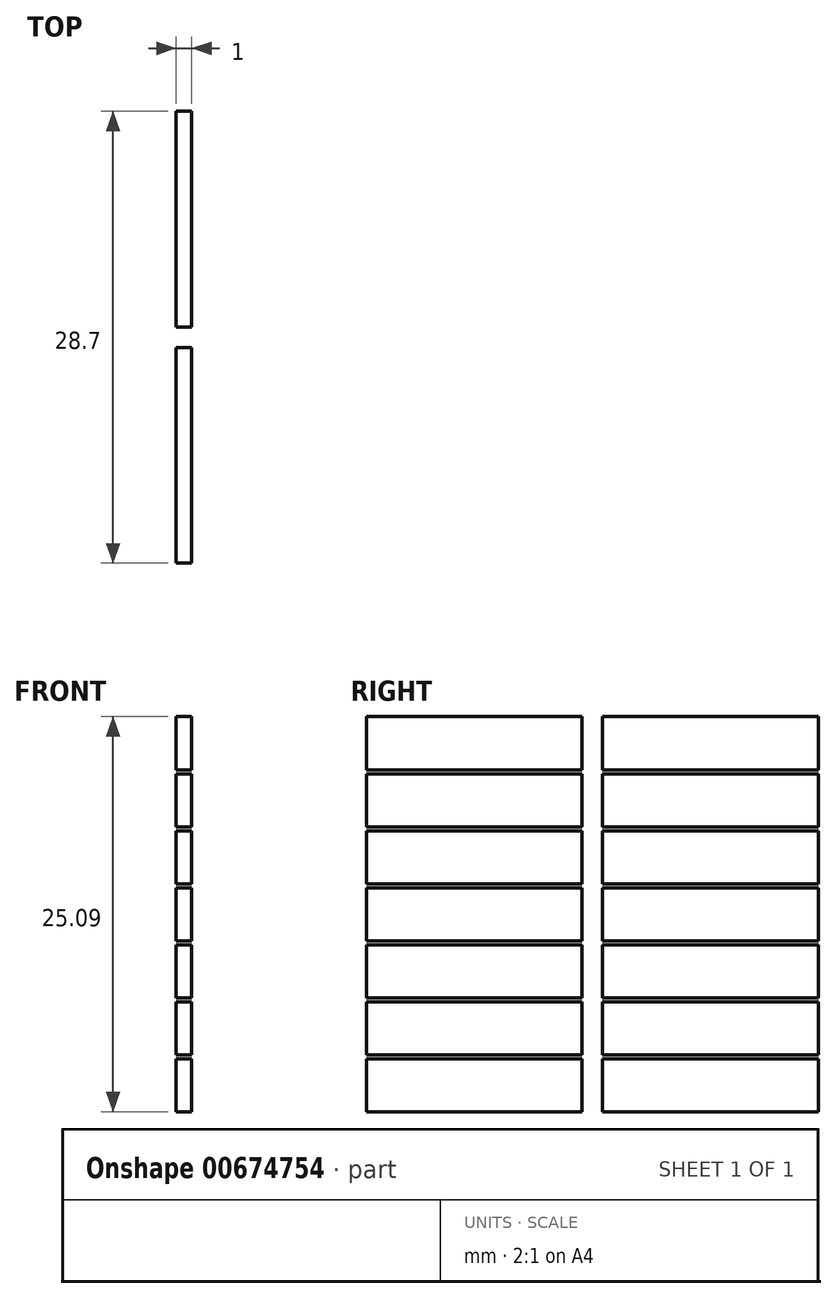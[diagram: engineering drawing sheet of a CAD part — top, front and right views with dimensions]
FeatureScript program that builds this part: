
annotation { "Feature Type Name" : "Feature", "Feature Type Description" : "" }
export const myFeature = defineFeature(function(context is Context, id is Id, definition is map)
    precondition{}
    {
        {
            var Q0;
            Q0=qCreatedBy(makeId("Right.planeOp"),FACE);
            var sketch = newSketch(context, id + "F0", { "sketchPlane" : qUnion([Q0])});
            skPoint(sketch, "E0.0", {"position": v(0, 0) * mm});
            skLineSegment(sketch, "E1.bottom", {"start": v(0, 0) * mm, "end": v(30, 0) * mm});
            skLineSegment(sketch, "E1.top", {"start": v(0, -30) * mm, "end": v(30, -30) * mm});
            skLineSegment(sketch, "E1.left", {"start": v(0, 0) * mm, "end": v(0, -30) * mm});
            skLineSegment(sketch, "E1.right", {"start": v(30, 0) * mm, "end": v(30, -30) * mm});
            skLineSegment(sketch, "E2.1", {"start": v(0.65, -0.65) * mm, "end": v(14.35, -0.65) * mm});
            skLineSegment(sketch, "E2.2", {"start": v(0.65, -0.65) * mm, "end": v(0.65, -2.2) * mm});
            skLineSegment(sketch, "E3", {"start": v(14.35, -2.2) * mm, "end": v(14.35, -0.65) * mm});
            skPoint(sketch, "E4.MirrorP", {"position": v(11.5, 0) * mm});
            skPoint(sketch, "E5.orphan", {"position": v(0, -26.74) * mm});
            skLineSegment(sketch, "E6", {"start": v(0.65, -2.46) * mm, "end": v(0.65, -4.02) * mm});
            skLineSegment(sketch, "E7", {"start": v(0.65, -4.02) * mm, "end": v(14.35, -4.02) * mm});
            skLineSegment(sketch, "E8", {"start": v(14.35, -4.02) * mm, "end": v(14.35, -2.46) * mm});
            skLineSegment(sketch, "E9.0", {"start": v(0.65, -4.27) * mm, "end": v(14.35, -4.27) * mm});
            skLineSegment(sketch, "E10", {"start": v(0.65, -4.27) * mm, "end": v(0.65, -5.83) * mm});
            skLineSegment(sketch, "E11", {"start": v(14.35, -5.83) * mm, "end": v(14.35, -4.27) * mm});
            skLineSegment(sketch, "E12.0", {"start": v(0.65, -7.64) * mm, "end": v(14.35, -7.64) * mm});
            skLineSegment(sketch, "E13", {"start": v(0.65, -6.08) * mm, "end": v(0.65, -7.64) * mm});
            skLineSegment(sketch, "E14", {"start": v(14.35, -6.08) * mm, "end": v(14.35, -7.64) * mm});
            skLineSegment(sketch, "E15.0", {"start": v(0.65, -7.9) * mm, "end": v(14.35, -7.9) * mm});
            skLineSegment(sketch, "E16", {"start": v(0.65, -7.9) * mm, "end": v(0.65, -9.45) * mm});
            skLineSegment(sketch, "E17", {"start": v(14.35, -9.45) * mm, "end": v(14.35, -7.9) * mm});
            skLineSegment(sketch, "E18.0", {"start": v(0.65, -11.26) * mm, "end": v(14.35, -11.26) * mm});
            skLineSegment(sketch, "E19", {"start": v(0.65, -9.7) * mm, "end": v(0.65, -11.26) * mm});
            skLineSegment(sketch, "E20", {"start": v(14.35, -9.7) * mm, "end": v(14.35, -11.26) * mm});
            skLineSegment(sketch, "E21.0", {"start": v(0.65, -11.51) * mm, "end": v(14.35, -11.51) * mm});
            skLineSegment(sketch, "E22", {"start": v(0.65, -11.51) * mm, "end": v(0.65, -13.07) * mm});
            skLineSegment(sketch, "E23", {"start": v(14.35, -13.07) * mm, "end": v(14.35, -11.51) * mm});
            skLineSegment(sketch, "E24.0", {"start": v(0.65, -14.88) * mm, "end": v(14.35, -14.88) * mm});
            skLineSegment(sketch, "E25", {"start": v(0.65, -13.32) * mm, "end": v(0.65, -14.88) * mm});
            skLineSegment(sketch, "E26", {"start": v(14.35, -14.88) * mm, "end": v(14.35, -13.32) * mm});
            skLineSegment(sketch, "E27.0", {"start": v(0.65, -15.13) * mm, "end": v(14.35, -15.13) * mm});
            skLineSegment(sketch, "E28", {"start": v(0.65, -15.13) * mm, "end": v(0.65, -16.7) * mm});
            skLineSegment(sketch, "E29", {"start": v(14.35, -16.7) * mm, "end": v(14.35, -15.13) * mm});
            skLineSegment(sketch, "E30.0", {"start": v(0.65, -18.5) * mm, "end": v(14.35, -18.5) * mm});
            skLineSegment(sketch, "E31", {"start": v(0.65, -16.7) * mm, "end": v(0.65, -18.5) * mm});
            skLineSegment(sketch, "E32", {"start": v(14.35, -18.5) * mm, "end": v(14.35, -16.94) * mm});
            skLineSegment(sketch, "E33.0", {"start": v(0.65, -18.75) * mm, "end": v(14.35, -18.75) * mm});
            skLineSegment(sketch, "E34", {"start": v(0.65, -18.75) * mm, "end": v(0.65, -20.31) * mm});
            skLineSegment(sketch, "E35", {"start": v(14.35, -18.75) * mm, "end": v(14.35, -20.31) * mm});
            skLineSegment(sketch, "E36.0", {"start": v(0.65, -22.12) * mm, "end": v(14.35, -22.12) * mm});
            skLineSegment(sketch, "E37", {"start": v(0.65, -20.56) * mm, "end": v(0.65, -22.12) * mm});
            skLineSegment(sketch, "E38", {"start": v(14.35, -20.56) * mm, "end": v(14.35, -22.12) * mm});
            skLineSegment(sketch, "E39.0", {"start": v(0.65, -22.37) * mm, "end": v(14.35, -22.37) * mm});
            skLineSegment(sketch, "E40", {"start": v(0.65, -22.37) * mm, "end": v(0.65, -23.93) * mm});
            skLineSegment(sketch, "E41", {"start": v(14.35, -22.37) * mm, "end": v(14.35, -23.93) * mm});
            skLineSegment(sketch, "E42.0", {"start": v(0.65, -25.74) * mm, "end": v(14.35, -25.74) * mm});
            skLineSegment(sketch, "E43", {"start": v(0.65, -24.18) * mm, "end": v(0.65, -25.74) * mm});
            skLineSegment(sketch, "E44", {"start": v(14.35, -24.18) * mm, "end": v(14.35, -25.74) * mm});
            skLineSegment(sketch, "E45", {"start": v(0.65, -2.46) * mm, "end": v(0.65, -2.2) * mm});
            skLineSegment(sketch, "E46", {"start": v(14.35, -2.46) * mm, "end": v(14.35, -2.2) * mm});
            skLineSegment(sketch, "E47", {"start": v(0.65, -6.08) * mm, "end": v(0.65, -5.83) * mm});
            skLineSegment(sketch, "E48", {"start": v(14.35, -6.08) * mm, "end": v(14.35, -5.83) * mm});
            skLineSegment(sketch, "E49", {"start": v(14.35, -24.18) * mm, "end": v(14.35, -23.93) * mm});
            skLineSegment(sketch, "E50", {"start": v(0.65, -24.18) * mm, "end": v(0.65, -23.93) * mm});
            skLineSegment(sketch, "E51", {"start": v(0.65, -20.56) * mm, "end": v(0.65, -20.31) * mm});
            skLineSegment(sketch, "E52", {"start": v(14.35, -20.56) * mm, "end": v(14.35, -20.31) * mm});
            skLineSegment(sketch, "E53", {"start": v(14.35, -16.94) * mm, "end": v(14.35, -16.7) * mm});
            skLineSegment(sketch, "E54", {"start": v(14.35, -13.32) * mm, "end": v(14.35, -13.07) * mm});
            skLineSegment(sketch, "E55", {"start": v(0.65, -13.32) * mm, "end": v(0.65, -13.07) * mm});
            skLineSegment(sketch, "E56", {"start": v(0.65, -9.7) * mm, "end": v(0.65, -9.45) * mm});
            skLineSegment(sketch, "E57", {"start": v(14.35, -9.7) * mm, "end": v(14.35, -9.45) * mm});
            skLineSegment(sketch, "E58.MirrorCS", {"start": v(29.35, -0.65) * mm, "end": v(29.35, -2.2) * mm});
            skLineSegment(sketch, "E59.MirrorCS", {"start": v(29.35, -2.46) * mm, "end": v(29.35, -2.2) * mm});
            skLineSegment(sketch, "E60.MirrorCS", {"start": v(29.35, -2.46) * mm, "end": v(29.35, -4.02) * mm});
            skLineSegment(sketch, "E61.MirrorCS", {"start": v(29.35, -20.56) * mm, "end": v(29.35, -22.12) * mm});
            skLineSegment(sketch, "E62.MirrorCS", {"start": v(15.65, -4.02) * mm, "end": v(15.65, -2.46) * mm});
            skLineSegment(sketch, "E63.MirrorCS", {"start": v(29.35, -20.56) * mm, "end": v(29.35, -20.31) * mm});
            skLineSegment(sketch, "E64.MirrorCS", {"start": v(29.35, -7.9) * mm, "end": v(29.35, -9.45) * mm});
            skLineSegment(sketch, "E65.MirrorCS", {"start": v(15.65, -16.7) * mm, "end": v(15.65, -15.13) * mm});
            skLineSegment(sketch, "E66.MirrorCS", {"start": v(29.35, -9.7) * mm, "end": v(29.35, -9.45) * mm});
            skLineSegment(sketch, "E67.MirrorCS", {"start": v(29.35, -6.08) * mm, "end": v(29.35, -5.83) * mm});
            skLineSegment(sketch, "E68.MirrorCS", {"start": v(15.65, -9.7) * mm, "end": v(15.65, -9.45) * mm});
            skLineSegment(sketch, "E69.MirrorCS", {"start": v(15.65, -22.37) * mm, "end": v(15.65, -23.93) * mm});
            skLineSegment(sketch, "E70.MirrorCS", {"start": v(29.35, -24.18) * mm, "end": v(29.35, -23.93) * mm});
            skLineSegment(sketch, "E71.MirrorCS", {"start": v(29.35, -4.27) * mm, "end": v(29.35, -5.83) * mm});
            skLineSegment(sketch, "E72.MirrorCS", {"start": v(15.65, -20.56) * mm, "end": v(15.65, -20.31) * mm});
            skLineSegment(sketch, "E73.MirrorCS", {"start": v(15.65, -9.45) * mm, "end": v(15.65, -7.9) * mm});
            skLineSegment(sketch, "E74.MirrorCS", {"start": v(29.35, -11.51) * mm, "end": v(29.35, -13.07) * mm});
            skLineSegment(sketch, "E75.MirrorCS", {"start": v(29.35, -13.32) * mm, "end": v(29.35, -13.07) * mm});
            skLineSegment(sketch, "E76.MirrorCS", {"start": v(15.65, -6.08) * mm, "end": v(15.65, -7.64) * mm});
            skLineSegment(sketch, "E77.MirrorCS", {"start": v(15.65, -14.88) * mm, "end": v(15.65, -13.32) * mm});
            skLineSegment(sketch, "E78.MirrorCS", {"start": v(29.35, -18.75) * mm, "end": v(29.35, -20.31) * mm});
            skLineSegment(sketch, "E79.MirrorCS", {"start": v(15.65, -24.18) * mm, "end": v(15.65, -23.93) * mm});
            skLineSegment(sketch, "E80.MirrorCS", {"start": v(29.35, -6.08) * mm, "end": v(29.35, -7.64) * mm});
            skLineSegment(sketch, "E81.MirrorCS", {"start": v(29.35, -13.32) * mm, "end": v(29.35, -14.88) * mm});
            skLineSegment(sketch, "E82.MirrorCS", {"start": v(15.65, -6.08) * mm, "end": v(15.65, -5.83) * mm});
            skLineSegment(sketch, "E83.MirrorCS", {"start": v(15.65, -18.5) * mm, "end": v(15.65, -16.94) * mm});
            skLineSegment(sketch, "E84.MirrorCS", {"start": v(29.35, -9.7) * mm, "end": v(29.35, -11.26) * mm});
            skLineSegment(sketch, "E85.MirrorCS", {"start": v(15.65, -13.07) * mm, "end": v(15.65, -11.51) * mm});
            skLineSegment(sketch, "E86.MirrorCS", {"start": v(15.65, -20.56) * mm, "end": v(15.65, -22.12) * mm});
            skLineSegment(sketch, "E87.MirrorCS", {"start": v(15.65, -13.32) * mm, "end": v(15.65, -13.07) * mm});
            skLineSegment(sketch, "E88.MirrorCS", {"start": v(15.65, -5.83) * mm, "end": v(15.65, -4.27) * mm});
            skLineSegment(sketch, "E89.MirrorCS", {"start": v(15.65, -9.7) * mm, "end": v(15.65, -11.26) * mm});
            skLineSegment(sketch, "E90.MirrorCS", {"start": v(29.35, -22.37) * mm, "end": v(29.35, -23.93) * mm});
            skLineSegment(sketch, "E91.MirrorCS", {"start": v(15.65, -18.75) * mm, "end": v(15.65, -20.31) * mm});
            skLineSegment(sketch, "E92.MirrorCS", {"start": v(29.35, -16.7) * mm, "end": v(29.35, -18.5) * mm});
            skLineSegment(sketch, "E93.MirrorCS", {"start": v(15.65, -2.2) * mm, "end": v(15.65, -0.65) * mm});
            skLineSegment(sketch, "E94.MirrorCS", {"start": v(29.35, -24.18) * mm, "end": v(29.35, -25.74) * mm});
            skLineSegment(sketch, "E95.MirrorCS", {"start": v(29.35, -15.13) * mm, "end": v(29.35, -16.7) * mm});
            skLineSegment(sketch, "E96.MirrorCS", {"start": v(15.65, -24.18) * mm, "end": v(15.65, -25.74) * mm});
            skLineSegment(sketch, "E97.MirrorCS", {"start": v(29.35, -4.02) * mm, "end": v(15.65, -4.02) * mm});
            skPoint(sketch, "E98.MirrorP", {"position": v(18.5, 0) * mm});
            skPoint(sketch, "E99.MirrorP", {"position": v(30, 0) * mm});
            skLineSegment(sketch, "E100.MirrorCS", {"start": v(29.35, -14.88) * mm, "end": v(15.65, -14.88) * mm});
            skLineSegment(sketch, "E101.MirrorCS", {"start": v(29.35, -0.65) * mm, "end": v(15.65, -0.65) * mm});
            skPoint(sketch, "E102.MirrorP", {"position": v(30, -26.74) * mm});
            skLineSegment(sketch, "E103.MirrorCS", {"start": v(29.35, -11.26) * mm, "end": v(15.65, -11.26) * mm});
            skLineSegment(sketch, "E104.MirrorCS", {"start": v(29.35, -18.75) * mm, "end": v(15.65, -18.75) * mm});
            skLineSegment(sketch, "E105.MirrorCS", {"start": v(29.35, -11.51) * mm, "end": v(15.65, -11.51) * mm});
            skLineSegment(sketch, "E106.MirrorCS", {"start": v(29.35, -22.37) * mm, "end": v(15.65, -22.37) * mm});
            skLineSegment(sketch, "E107.MirrorCS", {"start": v(29.35, -7.9) * mm, "end": v(15.65, -7.9) * mm});
            skLineSegment(sketch, "E108.MirrorCS", {"start": v(29.35, -25.74) * mm, "end": v(15.65, -25.74) * mm});
            skLineSegment(sketch, "E109.MirrorCS", {"start": v(29.35, -15.13) * mm, "end": v(15.65, -15.13) * mm});
            skLineSegment(sketch, "E110.MirrorCS", {"start": v(29.35, -4.27) * mm, "end": v(15.65, -4.27) * mm});
            skLineSegment(sketch, "E111.MirrorCS", {"start": v(29.35, -18.5) * mm, "end": v(15.65, -18.5) * mm});
            skLineSegment(sketch, "E112.MirrorCS", {"start": v(29.35, -7.64) * mm, "end": v(15.65, -7.64) * mm});
            skLineSegment(sketch, "E113.MirrorCS", {"start": v(29.35, -22.12) * mm, "end": v(15.65, -22.12) * mm});
            skLineSegment(sketch, "E114", {"start": v(15.65, -2.46) * mm, "end": v(15.65, -2.2) * mm});
            skLineSegment(sketch, "E115", {"start": v(15.65, -16.94) * mm, "end": v(15.65, -16.7) * mm});
            skSolve(sketch);
        }
        {
            var Q0;
            Q0=makeQuery(id+"F0.imprint","IMPRINT",FACE,{"disambiguationData":[TD([[makeQuery(id+"F0.imprint","IMPRINT",EDGE,{"derivedFrom":sQuery(id+"F0.wireOp",EDGE,"E69.MirrorCS")}),1.0]])]});
            var Q1;
            Q1=makeQuery(id+"F0.imprint","IMPRINT",FACE,{"disambiguationData":[TD([[makeQuery(id+"F0.imprint","IMPRINT",EDGE,{"derivedFrom":sQuery(id+"F0.wireOp",EDGE,"E61.MirrorCS")}),-1.0]])]});
            var Q2;
            Q2=makeQuery(id+"F0.imprint","IMPRINT",FACE,{"disambiguationData":[TD([[makeQuery(id+"F0.imprint","IMPRINT",EDGE,{"derivedFrom":sQuery(id+"F0.wireOp",EDGE,"E65.MirrorCS")}),-1.0]])]});
            var Q3;
            Q3=makeQuery(id+"F0.imprint","IMPRINT",FACE,{"disambiguationData":[TD([[makeQuery(id+"F0.imprint","IMPRINT",EDGE,{"derivedFrom":sQuery(id+"F0.wireOp",EDGE,"E74.MirrorCS")}),-1.0]])]});
            var Q4;
            Q4=makeQuery(id+"F0.imprint","IMPRINT",FACE,{"disambiguationData":[TD([[makeQuery(id+"F0.imprint","IMPRINT",EDGE,{"derivedFrom":sQuery(id+"F0.wireOp",EDGE,"E64.MirrorCS")}),-1.0]])]});
            var Q5;
            Q5=makeQuery(id+"F0.imprint","IMPRINT",FACE,{"disambiguationData":[TD([[makeQuery(id+"F0.imprint","IMPRINT",EDGE,{"derivedFrom":sQuery(id+"F0.wireOp",EDGE,"E67.MirrorCS")}),1.0]])]});
            var Q6;
            Q6=makeQuery(id+"F0.imprint","IMPRINT",FACE,{"disambiguationData":[TD([[makeQuery(id+"F0.imprint","IMPRINT",EDGE,{"derivedFrom":sQuery(id+"F0.wireOp",EDGE,"E59.MirrorCS")}),1.0]])]});
            var Q7;
            Q7=makeQuery(id+"F0.imprint","IMPRINT",FACE,{"disambiguationData":[TD([[makeQuery(id+"F0.imprint","IMPRINT",EDGE,{"derivedFrom":sQuery(id+"F0.wireOp",EDGE,"E2.1")}),-1.0]])]});
            var Q8;
            Q8=makeQuery(id+"F0.imprint","IMPRINT",FACE,{"disambiguationData":[TD([[makeQuery(id+"F0.imprint","IMPRINT",EDGE,{"derivedFrom":sQuery(id+"F0.wireOp",EDGE,"E9.0")}),-1.0]])]});
            var Q9;
            Q9=makeQuery(id+"F0.imprint","IMPRINT",FACE,{"disambiguationData":[TD([[makeQuery(id+"F0.imprint","IMPRINT",EDGE,{"derivedFrom":sQuery(id+"F0.wireOp",EDGE,"E15.0")}),-1.0]])]});
            var Q10;
            Q10=makeQuery(id+"F0.imprint","IMPRINT",FACE,{"disambiguationData":[TD([[makeQuery(id+"F0.imprint","IMPRINT",EDGE,{"derivedFrom":sQuery(id+"F0.wireOp",EDGE,"E21.0")}),-1.0]])]});
            var Q11;
            Q11=makeQuery(id+"F0.imprint","IMPRINT",FACE,{"disambiguationData":[TD([[makeQuery(id+"F0.imprint","IMPRINT",EDGE,{"derivedFrom":sQuery(id+"F0.wireOp",EDGE,"E27.0")}),-1.0]])]});
            var Q12;
            Q12=makeQuery(id+"F0.imprint","IMPRINT",FACE,{"disambiguationData":[TD([[makeQuery(id+"F0.imprint","IMPRINT",EDGE,{"derivedFrom":sQuery(id+"F0.wireOp",EDGE,"E33.0")}),-1.0]])]});
            var Q13;
            Q13=makeQuery(id+"F0.imprint","IMPRINT",FACE,{"disambiguationData":[TD([[makeQuery(id+"F0.imprint","IMPRINT",EDGE,{"derivedFrom":sQuery(id+"F0.wireOp",EDGE,"E39.0")}),-1.0]])]});
            extrude(context, id + "F1", {"entities" : qUnion([Q0, Q1, Q2, Q3, Q4, Q5, Q6, Q7, Q8, Q9, Q10, Q11, Q12, Q13]), "depth" : 1 * mm, "offsetDistance" : 25 * mm});
        }
    });
